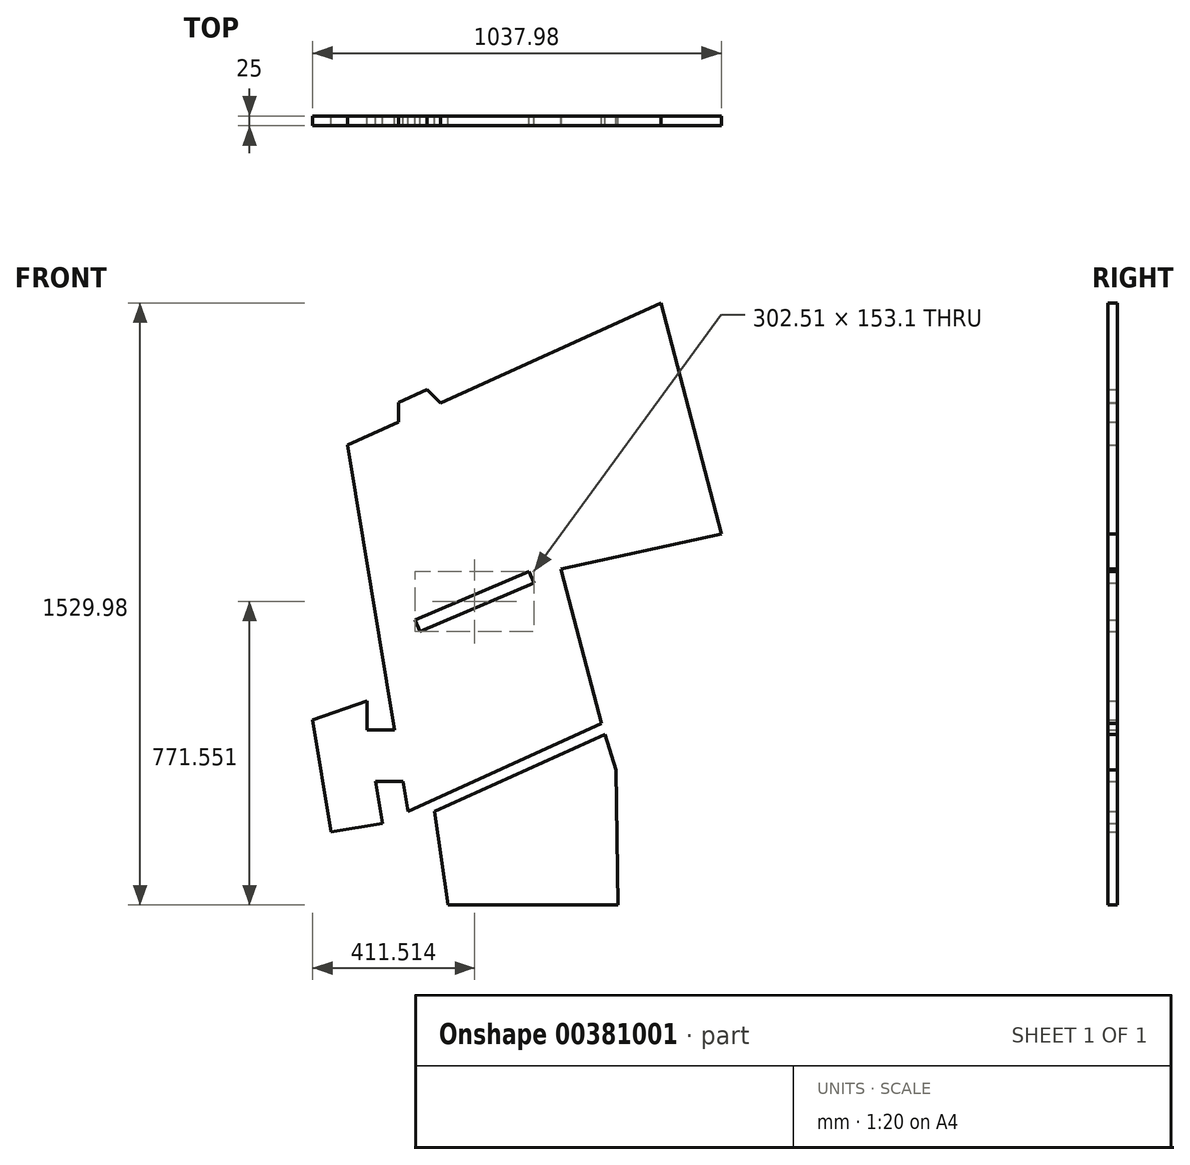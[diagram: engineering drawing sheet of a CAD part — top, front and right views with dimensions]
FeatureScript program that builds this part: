
annotation { "Feature Type Name" : "Feature", "Feature Type Description" : "" }
export const myFeature = defineFeature(function(context is Context, id is Id, definition is map)
    precondition{}
    {
        {
            var Q0;
            Q0=qCreatedBy(makeId("Front.planeOp"),FACE);
            var sketch = newSketch(context, id + "F0", { "sketchPlane" : qUnion([Q0])});
            skLineSegment(sketch, "E0", {"start": v(0, 0) * mm, "end": v(-34.35, 237.53) * mm});
            skLineSegment(sketch, "E1", {"start": v(-34.35, 237.53) * mm, "end": v(398.28, 433.64) * mm});
            skLineSegment(sketch, "E2", {"start": v(398.28, 433.64) * mm, "end": v(426.63, 342.97) * mm});
            skLineSegment(sketch, "E3", {"start": v(426.63, 342.97) * mm, "end": v(431, 0) * mm});
            skLineSegment(sketch, "E4", {"start": v(431, 0) * mm, "end": v(285, 0) * mm});
            skLineSegment(sketch, "E5", {"start": v(285, 0) * mm, "end": v(0, 0) * mm});
            skLineSegment(sketch, "E6", {"start": v(285, 0) * mm, "end": v(204.28, 345.7) * mm});
            skLineSegment(sketch, "E7", {"start": v(-102.28, 238.34) * mm, "end": v(389.62, 461.32) * mm});
            skLineSegment(sketch, "E8", {"start": v(389.62, 461.32) * mm, "end": v(398.28, 433.64) * mm});
            skLineSegment(sketch, "E9", {"start": v(-102.28, 238.34) * mm, "end": v(-170.77, 652.72) * mm});
            skLineSegment(sketch, "E10", {"start": v(-170.77, 652.72) * mm, "end": v(287.34, 848.02) * mm});
            skLineSegment(sketch, "E11", {"start": v(287.34, 848.02) * mm, "end": v(389.62, 461.32) * mm});
            skLineSegment(sketch, "E12", {"start": v(213.39, 349.83) * mm, "end": v(295, 0) * mm});
            skPoint(sketch, "E12.startSnap0", {"position": v(143.67, 349.83) * mm});
            skLineSegment(sketch, "E13", {"start": v(-170.77, 652.72) * mm, "end": v(-176.15, 685.28) * mm});
            skLineSegment(sketch, "E14", {"start": v(-176.15, 685.28) * mm, "end": v(-256.05, 1168.72) * mm});
            skLineSegment(sketch, "E15", {"start": v(-256.05, 1168.72) * mm, "end": v(92.78, 1326.85) * mm});
            skLineSegment(sketch, "E16", {"start": v(240.32, 862.83) * mm, "end": v(-176.15, 685.28) * mm});
            skLineSegment(sketch, "E17", {"start": v(92.78, 1326.85) * mm, "end": v(142.87, 1349.55) * mm});
            skLineSegment(sketch, "E18", {"start": v(-256.05, 1168.72) * mm, "end": v(-125.8, 1227.76) * mm});
            skLineSegment(sketch, "E19", {"start": v(-125.8, 1227.76) * mm, "end": v(-125.8, 1277.16) * mm});
            skLineSegment(sketch, "E20", {"start": v(-125.8, 1277.16) * mm, "end": v(-54.41, 1309.53) * mm});
            skLineSegment(sketch, "E21", {"start": v(-54.41, 1309.53) * mm, "end": v(-19.25, 1276.06) * mm});
            skLineSegment(sketch, "E22", {"start": v(-19.25, 1276.06) * mm, "end": v(92.78, 1326.85) * mm});
            skLineSegment(sketch, "E23", {"start": v(142.87, 1349.55) * mm, "end": v(540.9, 1529.98) * mm});
            skLineSegment(sketch, "E24", {"start": v(540.9, 1529.98) * mm, "end": v(693.56, 942.49) * mm});
            skLineSegment(sketch, "E25", {"start": v(693.56, 942.49) * mm, "end": v(287.06, 854.07) * mm});
            skLineSegment(sketch, "E26", {"start": v(287.06, 854.07) * mm, "end": v(287.34, 848.02) * mm});
            skLineSegment(sketch, "E27", {"start": v(693.56, 942.49) * mm, "end": v(678.72, 999.6) * mm});
            skLineSegment(sketch, "E28", {"start": v(92.78, 1326.85) * mm, "end": v(227.9, 968.47) * mm});
            skLineSegment(sketch, "E29", {"start": v(227.9, 968.47) * mm, "end": v(279.25, 987.83) * mm});
            skLineSegment(sketch, "E30", {"start": v(142.87, 1349.55) * mm, "end": v(279.25, 987.83) * mm});
            skLineSegment(sketch, "E31", {"start": v(259.15, 884.07) * mm, "end": v(291.67, 855.24) * mm});
            skLineSegment(sketch, "E32", {"start": v(291.67, 855.24) * mm, "end": v(287.06, 854.07) * mm});
            skLineSegment(sketch, "E33", {"start": v(259.15, 884.07) * mm, "end": v(240.32, 862.83) * mm});
            skLineSegment(sketch, "E34", {"start": v(-125.8, 1277.16) * mm, "end": v(-410.26, 1141.17) * mm});
            skLineSegment(sketch, "E35", {"start": v(-54.41, 1309.53) * mm, "end": v(601.84, 1607.01) * mm});
            skLineSegment(sketch, "E36", {"start": v(355.15, 591.65) * mm, "end": v(288.96, 415.69) * mm});
            skLineSegment(sketch, "E37", {"start": v(-102.28, 238.34) * mm, "end": v(-114.84, 314.34) * mm});
            skLineSegment(sketch, "E38", {"start": v(-114.84, 314.34) * mm, "end": v(-184.84, 314.34) * mm});
            skLineSegment(sketch, "E39", {"start": v(-184.84, 314.34) * mm, "end": v(-167.23, 207.78) * mm});
            skLineSegment(sketch, "E40", {"start": v(-167.23, 207.78) * mm, "end": v(-297.46, 186.26) * mm});
            skLineSegment(sketch, "E41", {"start": v(-297.46, 186.26) * mm, "end": v(-344.42, 470.4) * mm});
            skLineSegment(sketch, "E42", {"start": v(-344.42, 470.4) * mm, "end": v(-206.7, 518.86) * mm});
            skLineSegment(sketch, "E43", {"start": v(-206.7, 518.86) * mm, "end": v(-206.7, 445.28) * mm});
            skLineSegment(sketch, "E44", {"start": v(-206.7, 445.28) * mm, "end": v(-136.48, 445.28) * mm});
            skLineSegment(sketch, "E45", {"start": v(-84.16, 724.5) * mm, "end": v(109.02, 806.85) * mm});
            skLineSegment(sketch, "E46", {"start": v(-170.77, 652.72) * mm, "end": v(133.72, 782.53) * mm});
            skLineSegment(sketch, "E47", {"start": v(133.72, 782.53) * mm, "end": v(121.14, 812.02) * mm});
            skLineSegment(sketch, "E48", {"start": v(287.34, 848.02) * mm, "end": v(218.35, 818.6) * mm});
            skLineSegment(sketch, "E49", {"start": v(218.35, 818.6) * mm, "end": v(205.77, 848.1) * mm});
            skLineSegment(sketch, "E50", {"start": v(-84.16, 724.5) * mm, "end": v(-71.58, 695) * mm});
            skLineSegment(sketch, "E51", {"start": v(143, 0) * mm, "end": v(280, 0) * mm});
            skLineSegment(sketch, "E52", {"start": v(143, 0) * mm, "end": v(143, -30) * mm});
            skLineSegment(sketch, "E53", {"start": v(143, -30) * mm, "end": v(-95.2, -30) * mm});
            skLineSegment(sketch, "E54", {"start": v(280, 0) * mm, "end": v(280, -30) * mm});
            skLineSegment(sketch, "E55", {"start": v(280, -30) * mm, "end": v(606.73, -30) * mm});
            skSolve(sketch);
        }
        {
            var Q0;
            Q0 = qSketchRegion(id + "F0", true);
            extrude(context, id + "F1", {"entities" : qUnion([Q0]), "depth" : 25 * mm});
        }
    });
